# Revit family: LEGRAND_TOMAS SIN ENCLAVAMIENTO_EMPOTRADAS_IP44_440
name_source: partatom
category: Installations électriques
revit_build: Autodesk Revit 2018 (Build: 20170223_1515(x64)
units: mm (PartAtom-declared; Revit-internal decimal feet)

## family parameters
Conserver l'orientation des annotations = Non
Cote de connecteur circulaire = Utiliser le diamètre
Couper avec des vides une fois chargée = Non
Hôte = Face
Partagée = Non
Point de calcul de pièce = Non
Type d'élément = Normal

## types (3) — shared parameters
Condiciones Generales de Uso = https://export.legrand.com
Description = Toma AL estándar internacional para montaje empotrado o en superficie con accesorio permite la alimentación de aparatos de potencia
Elévation par défaut = 1000 mm  [stored 3.28084 ft]
Estándar CEI o NFC = CEI
Fabricant = Legrand
Temperatura maxima de instalación = 40°C
Temperatura maxima de uso = 100°C
Temperatura minima de instalación = -20°C
Temperatura minima de uso = -50°C
Tension V = 400 440 V  50 60 Hz rojo
color característico = rojo
distancia de fijación vertical mm = 70 mm
instalación de empotrar E o de superficie S = empotrar y superficie
materia de la caja = plástico
numero de polos = 4
resistencia a los choques IK = 09
tipo de conexión = conexión por tonillo

## per-type parameters (varying)
| type | Dia bouchon | Modèle | RAY BOUCHON | Ray | altura mm | ancho mm | clase de protección IP | distancia de fijación horizontal mm | h1 | intensidad A | posición de la tierra h | profundidad de empotrar mm | profundidad mm | sin halogeno |
| base para cuadro Hypra   IP44   MBT 16 A   440/460 V   2P+T   plast | 48 mm | 052310 | 24 mm | 24 mm | 84 mm | 74 mm | IP44 | 60 mm | 50 mm | 16 A | 11 | 44 mm | 84 mm | Oui |
| base para cuadro à entreejes unificados Hypra   IP44   32 A   440/460 V   3P+T   plast | 55 mm | 052350 | 27 mm | 27 mm | 94 mm | 84 mm | IP44 | 70 mm | 56 mm | 32 A | 11 | 50 mm | 99 mm | Oui |
| base para cuadro entreejes unificados Hypra IP6/ 67-55 32A 440V conteneur frigo 3P+T plast | 55 mm | 052926 | 27 mm | 27 mm | 94 mm | 84 mm | IP66/67-55 | 70 mm | 56 mm | 32 A | 3 | 54 mm | 104 mm | Non |

note: [stored X ft] marks values corroborated as IEEE doubles in the binary element streams (Revit-internal decimal feet)
